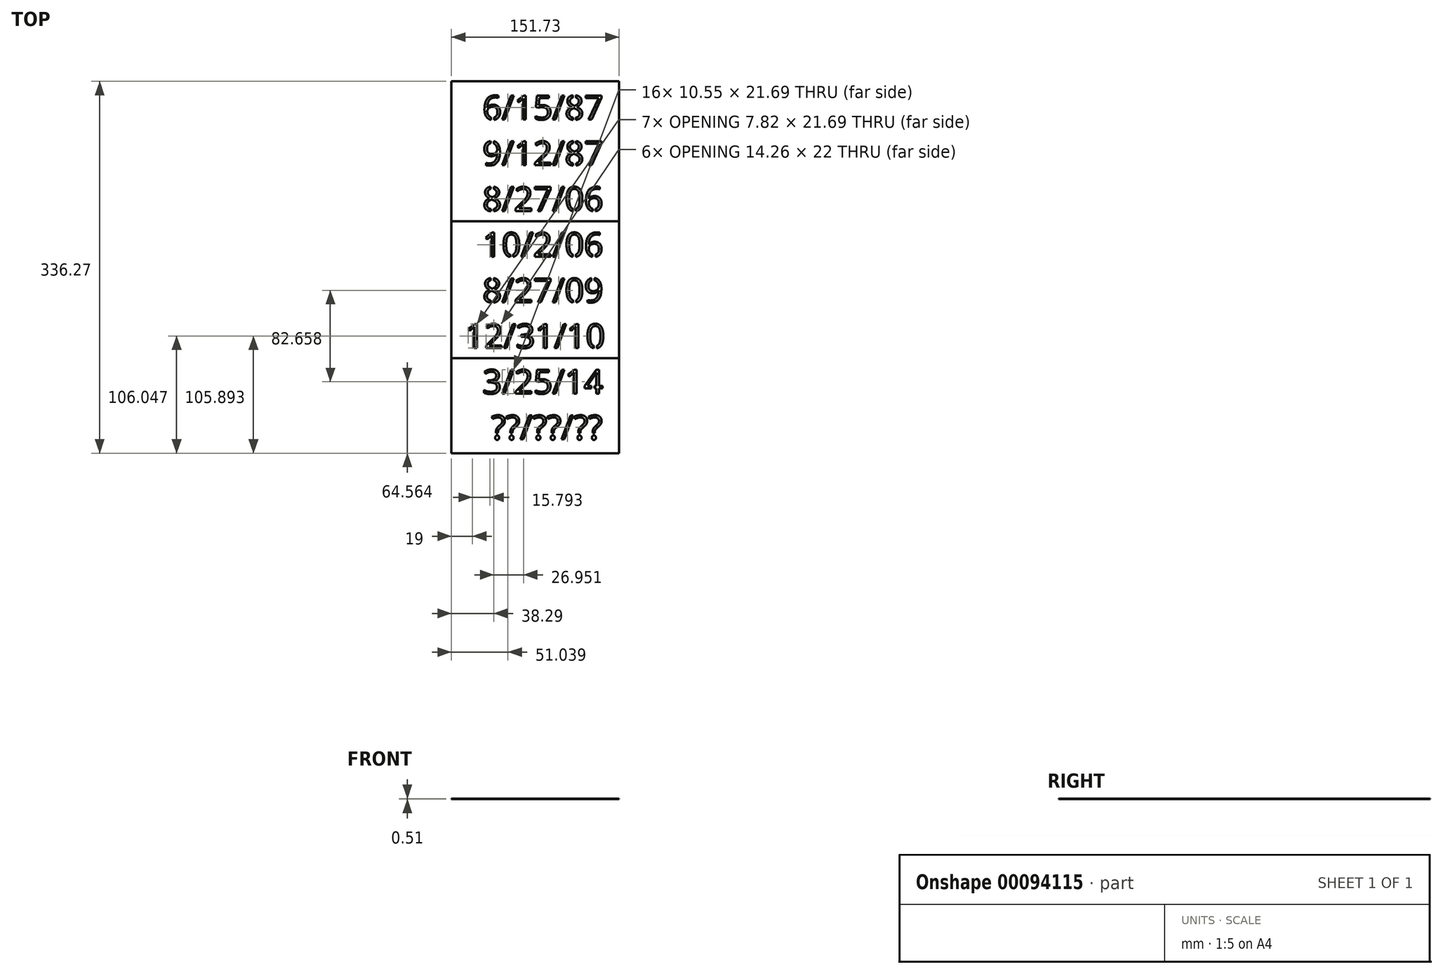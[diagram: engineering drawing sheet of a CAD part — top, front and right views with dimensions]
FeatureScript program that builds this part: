
annotation { "Feature Type Name" : "Feature", "Feature Type Description" : "" }
export const myFeature = defineFeature(function(context is Context, id is Id, definition is map)
    precondition{}
    {
        {
            var Q0;
            Q0=qCreatedBy(makeId("Top.planeOp"),FACE);
            var sketch = newSketch(context, id + "F0", { "sketchPlane" : qUnion([Q0])});
            skText(sketch, "E0", { "text": "  6/15/87\n  9/12/87\n  8/27/06\n  10/2/06\n  8/27/09\n12/31/10\n  3/25/14\n   ??/??/??", "fontName": "OpenSans-Regular.ttf"});
            skLineSegment(sketch, "E1.bottom", {"start": v(-12.3, 34.58) * mm, "end": v(139.43, 34.58) * mm});
            skLineSegment(sketch, "E1.top", {"start": v(-12.3, -301.7) * mm, "end": v(139.43, -301.7) * mm});
            skLineSegment(sketch, "E1.left", {"start": v(-12.3, 34.58) * mm, "end": v(-12.3, -301.7) * mm});
            skLineSegment(sketch, "E1.right", {"start": v(139.43, 34.58) * mm, "end": v(139.43, -301.7) * mm});
            skLineSegment(sketch, "E2", {"start": v(-12.3, -91.86) * mm, "end": v(139.43, -91.86) * mm});
            skLineSegment(sketch, "E3", {"start": v(-12.3, -215.95) * mm, "end": v(139.43, -215.95) * mm});
            skLineSegment(sketch, "E4.left", {"start": v(23.37, 3.55) * mm, "end": v(23.37, -2.65) * mm});
            skLineSegment(sketch, "E4.right", {"start": v(26.12, 3.55) * mm, "end": v(26.12, -2.65) * mm});
            skLineSegment(sketch, "E5.left", {"start": v(97.64, 3.6) * mm, "end": v(97.64, -2.6) * mm});
            skLineSegment(sketch, "E5.right", {"start": v(100.4, 3.6) * mm, "end": v(100.4, -2.6) * mm});
            skLineSegment(sketch, "E6.left", {"start": v(97.5, 23.74) * mm, "end": v(97.5, 17.54) * mm});
            skLineSegment(sketch, "E6.right", {"start": v(100.25, 23.74) * mm, "end": v(100.25, 17.54) * mm});
            skLineSegment(sketch, "E7.left", {"start": v(23.05, -16.8) * mm, "end": v(23.05, -23) * mm});
            skLineSegment(sketch, "E7.right", {"start": v(25.8, -16.8) * mm, "end": v(25.8, -23) * mm});
            skLineSegment(sketch, "E8.left", {"start": v(97.72, -37.6) * mm, "end": v(97.72, -43.8) * mm});
            skLineSegment(sketch, "E8.right", {"start": v(100.47, -37.6) * mm, "end": v(100.47, -43.8) * mm});
            skLineSegment(sketch, "E9.left", {"start": v(97.58, -17.46) * mm, "end": v(97.58, -23.66) * mm});
            skLineSegment(sketch, "E9.right", {"start": v(100.33, -17.46) * mm, "end": v(100.33, -23.66) * mm});
            skLineSegment(sketch, "E10.left", {"start": v(23.27, -79.53) * mm, "end": v(23.27, -85.73) * mm});
            skLineSegment(sketch, "E10.right", {"start": v(26.03, -79.53) * mm, "end": v(26.03, -85.73) * mm});
            skLineSegment(sketch, "E11.left", {"start": v(23.13, -59.4) * mm, "end": v(23.13, -65.6) * mm});
            skLineSegment(sketch, "E11.right", {"start": v(25.89, -59.4) * mm, "end": v(25.89, -65.6) * mm});
            skLineSegment(sketch, "E12.left", {"start": v(115.4, -78.82) * mm, "end": v(115.4, -85.02) * mm});
            skLineSegment(sketch, "E12.right", {"start": v(118.15, -78.82) * mm, "end": v(118.15, -85.02) * mm});
            skLineSegment(sketch, "E13.left", {"start": v(97.58, -78.61) * mm, "end": v(97.58, -84.8) * mm});
            skLineSegment(sketch, "E13.right", {"start": v(100.33, -78.61) * mm, "end": v(100.33, -84.8) * mm});
            skLineSegment(sketch, "E14.left", {"start": v(40.8, -120.16) * mm, "end": v(40.8, -126.36) * mm});
            skLineSegment(sketch, "E14.right", {"start": v(43.56, -120.16) * mm, "end": v(43.56, -126.36) * mm});
            skLineSegment(sketch, "E15.left", {"start": v(97.56, -120.04) * mm, "end": v(97.56, -126.23) * mm});
            skLineSegment(sketch, "E15.right", {"start": v(100.31, -120.04) * mm, "end": v(100.31, -126.23) * mm});
            skLineSegment(sketch, "E16.left", {"start": v(115.23, -119.9) * mm, "end": v(115.23, -126.1) * mm});
            skLineSegment(sketch, "E16.right", {"start": v(117.98, -119.9) * mm, "end": v(117.98, -126.1) * mm});
            skLineSegment(sketch, "E17.left", {"start": v(97.82, -161.57) * mm, "end": v(97.82, -167.76) * mm});
            skLineSegment(sketch, "E17.right", {"start": v(100.57, -161.57) * mm, "end": v(100.57, -167.76) * mm});
            skLineSegment(sketch, "E18.left", {"start": v(114.33, -141.06) * mm, "end": v(114.33, -147.26) * mm});
            skLineSegment(sketch, "E18.right", {"start": v(117.08, -141.06) * mm, "end": v(117.08, -147.26) * mm});
            skLineSegment(sketch, "E19.left", {"start": v(23.14, -141.32) * mm, "end": v(23.14, -147.52) * mm});
            skLineSegment(sketch, "E19.right", {"start": v(25.9, -141.32) * mm, "end": v(25.9, -147.52) * mm});
            skLineSegment(sketch, "E20.left", {"start": v(23.14, -161.7) * mm, "end": v(23.14, -167.9) * mm});
            skLineSegment(sketch, "E20.right", {"start": v(25.9, -161.7) * mm, "end": v(25.9, -167.9) * mm});
            skLineSegment(sketch, "E21.left", {"start": v(114.19, -238.95) * mm, "end": v(114.19, -245.15) * mm});
            skLineSegment(sketch, "E21.right", {"start": v(116.94, -238.95) * mm, "end": v(116.94, -245.15) * mm});
            skLineSegment(sketch, "E22.left", {"start": v(116.57, -202.43) * mm, "end": v(116.57, -208.63) * mm});
            skLineSegment(sketch, "E22.right", {"start": v(119.32, -202.43) * mm, "end": v(119.32, -208.63) * mm});
            const initialGuessF0  = {"E0": [0, 0, 1, 0, 0.02188]};
            skSetInitialGuess(sketch, initialGuessF0);
            skSolve(sketch);
        }
        {
            var Q0;
            Q0=makeQuery(id+"F0.imprint","IMPRINT",FACE,{"disambiguationData":[TD([[makeQuery(id+"F0.imprint","IMPRINT",EDGE,{"derivedFrom":sQuery(id+"F0.wireOp",EDGE,"E0.sketch_text.stroke-0")}),1.0]])]});
            var Q1;
            {var subQ0=sQuery(id+"F0.wireOp",EDGE,"E0.sketch_text.stroke-224");Q1=makeQuery(id+"F0.imprint","IMPRINT",FACE,{"disambiguationData":[TD([[makeQuery(id+"F0.imprint","IMPRINT",EDGE,{"derivedFrom":subQ0}),1.0]])]});}
            var Q2;
            {var subQ5=sQuery(id+"F0.wireOp",EDGE,"E0.sketch_text.stroke-215");Q2=makeQuery(id+"F0.imprint","IMPRINT",FACE,{"disambiguationData":[TD([[makeQuery(id+"F0.imprint","IMPRINT",EDGE,{"derivedFrom":subQ5}),1.0]])]});}
            var Q3;
            {var subQ5=sQuery(id+"F0.wireOp",EDGE,"E0.sketch_text.stroke-274");Q3=makeQuery(id+"F0.imprint","IMPRINT",FACE,{"disambiguationData":[TD([[makeQuery(id+"F0.imprint","IMPRINT",EDGE,{"derivedFrom":subQ5}),1.0]])]});}
            var Q4;
            {var subQ6=sQuery(id+"F0.wireOp",EDGE,"E0.sketch_text.stroke-298");Q4=makeQuery(id+"F0.imprint","IMPRINT",FACE,{"disambiguationData":[TD([[makeQuery(id+"F0.imprint","IMPRINT",EDGE,{"derivedFrom":subQ6}),1.0]])]});}
            var Q5;
            {var subQ5=sQuery(id+"F0.wireOp",EDGE,"E0.sketch_text.stroke-177");Q5=makeQuery(id+"F0.imprint","IMPRINT",FACE,{"disambiguationData":[TD([[makeQuery(id+"F0.imprint","IMPRINT",EDGE,{"derivedFrom":subQ5}),1.0]])]});}
            var Q6;
            {var subQ0=sQuery(id+"F0.wireOp",EDGE,"E0.sketch_text.stroke-186");Q6=makeQuery(id+"F0.imprint","IMPRINT",FACE,{"disambiguationData":[TD([[makeQuery(id+"F0.imprint","IMPRINT",EDGE,{"derivedFrom":subQ0}),1.0]])]});}
            var Q7;
            {var subQ1=sQuery(id+"F0.wireOp",EDGE,"E0.sketch_text.stroke-116");Q7=makeQuery(id+"F0.imprint","IMPRINT",FACE,{"disambiguationData":[TD([[makeQuery(id+"F0.imprint","IMPRINT",EDGE,{"derivedFrom":subQ1}),1.0]])]});}
            var Q8;
            {var subQ5=sQuery(id+"F0.wireOp",EDGE,"E0.sketch_text.stroke-16");Q8=makeQuery(id+"F0.imprint","IMPRINT",FACE,{"disambiguationData":[TD([[makeQuery(id+"F0.imprint","IMPRINT",EDGE,{"derivedFrom":subQ5}),1.0]])]});}
            var Q9;
            {var subQ0=sQuery(id+"F0.wireOp",EDGE,"E0.sketch_text.stroke-85");Q9=makeQuery(id+"F0.imprint","IMPRINT",FACE,{"disambiguationData":[TD([[makeQuery(id+"F0.imprint","IMPRINT",EDGE,{"derivedFrom":subQ0}),1.0]])]});}
            var Q10;
            {var subQ5=sQuery(id+"F0.wireOp",EDGE,"E0.sketch_text.stroke-76");Q10=makeQuery(id+"F0.imprint","IMPRINT",FACE,{"disambiguationData":[TD([[makeQuery(id+"F0.imprint","IMPRINT",EDGE,{"derivedFrom":subQ5}),1.0]])]});}
            var Q11;
            {var subQ5=sQuery(id+"F0.wireOp",EDGE,"E0.sketch_text.stroke-13");var subQ6=sQuery(id+"F0.wireOp",EDGE,"E0.sketch_text.stroke-12");var subQ7=makeQuery(id+"F0.imprint","INTERSECT",VERTEX,{"derivedFrom":[subQ6,subQ5]});Q11=makeQuery(id+"F0.imprint","IMPRINT",FACE,{"disambiguationData":[TD([[makeQuery(id+"F0.imprint","IMPRINT",EDGE,{"disambiguationData":[TD([[subQ7,1.0]])],"derivedFrom":subQ6}),-1.0]])]});}
            var Q12;
            {var subQ5=sQuery(id+"F0.wireOp",EDGE,"E0.sketch_text.stroke-75");var subQ6=sQuery(id+"F0.wireOp",EDGE,"E0.sketch_text.stroke-61");var subQ7=makeQuery(id+"F0.imprint","INTERSECT",VERTEX,{"derivedFrom":[subQ6,subQ5]});Q12=makeQuery(id+"F0.imprint","IMPRINT",FACE,{"disambiguationData":[TD([[makeQuery(id+"F0.imprint","IMPRINT",EDGE,{"disambiguationData":[TD([[subQ7,-1.0]])],"derivedFrom":subQ6}),-1.0]])]});}
            var Q13;
            {var subQ7=sQuery(id+"F0.wireOp",EDGE,"E0.sketch_text.stroke-69");var subQ8=sQuery(id+"F0.wireOp",EDGE,"E0.sketch_text.stroke-68");var subQ9=makeQuery(id+"F0.imprint","INTERSECT",VERTEX,{"derivedFrom":[subQ8,subQ7]});Q13=makeQuery(id+"F0.imprint","IMPRINT",FACE,{"disambiguationData":[TD([[makeQuery(id+"F0.imprint","IMPRINT",EDGE,{"disambiguationData":[TD([[subQ9,1.0]])],"derivedFrom":subQ8}),-1.0]])]});}
            var Q14;
            {var subQ7=sQuery(id+"F0.wireOp",EDGE,"E0.sketch_text.stroke-176");var subQ8=sQuery(id+"F0.wireOp",EDGE,"E0.sketch_text.stroke-162");var subQ9=makeQuery(id+"F0.imprint","INTERSECT",VERTEX,{"derivedFrom":[subQ8,subQ7]});Q14=makeQuery(id+"F0.imprint","IMPRINT",FACE,{"disambiguationData":[TD([[makeQuery(id+"F0.imprint","IMPRINT",EDGE,{"disambiguationData":[TD([[subQ9,-1.0]])],"derivedFrom":subQ8}),-1.0]])]});}
            var Q15;
            {var subQ7=sQuery(id+"F0.wireOp",EDGE,"E0.sketch_text.stroke-112");var subQ8=sQuery(id+"F0.wireOp",EDGE,"E0.sketch_text.stroke-111");var subQ9=makeQuery(id+"F0.imprint","INTERSECT",VERTEX,{"derivedFrom":[subQ8,subQ7]});Q15=makeQuery(id+"F0.imprint","IMPRINT",FACE,{"disambiguationData":[TD([[makeQuery(id+"F0.imprint","IMPRINT",EDGE,{"disambiguationData":[TD([[subQ9,1.0]])],"derivedFrom":subQ8}),-1.0]])]});}
            var Q16;
            {var subQ7=sQuery(id+"F0.wireOp",EDGE,"E0.sketch_text.stroke-170");var subQ8=sQuery(id+"F0.wireOp",EDGE,"E0.sketch_text.stroke-169");var subQ9=makeQuery(id+"F0.imprint","INTERSECT",VERTEX,{"derivedFrom":[subQ8,subQ7]});Q16=makeQuery(id+"F0.imprint","IMPRINT",FACE,{"disambiguationData":[TD([[makeQuery(id+"F0.imprint","IMPRINT",EDGE,{"disambiguationData":[TD([[subQ9,1.0]])],"derivedFrom":subQ8}),-1.0]])]});}
            var Q17;
            {var subQ5=sQuery(id+"F0.wireOp",EDGE,"E0.sketch_text.stroke-295");var subQ6=sQuery(id+"F0.wireOp",EDGE,"E0.sketch_text.stroke-294");var subQ7=makeQuery(id+"F0.imprint","INTERSECT",VERTEX,{"derivedFrom":[subQ6,subQ5]});Q17=makeQuery(id+"F0.imprint","IMPRINT",FACE,{"disambiguationData":[TD([[makeQuery(id+"F0.imprint","IMPRINT",EDGE,{"disambiguationData":[TD([[subQ7,1.0]])],"derivedFrom":subQ6}),-1.0]])]});}
            var Q18;
            {var subQ7=sQuery(id+"F0.wireOp",EDGE,"E0.sketch_text.stroke-268");var subQ8=sQuery(id+"F0.wireOp",EDGE,"E0.sketch_text.stroke-267");var subQ9=makeQuery(id+"F0.imprint","INTERSECT",VERTEX,{"derivedFrom":[subQ8,subQ7]});Q18=makeQuery(id+"F0.imprint","IMPRINT",FACE,{"disambiguationData":[TD([[makeQuery(id+"F0.imprint","IMPRINT",EDGE,{"disambiguationData":[TD([[subQ9,1.0]])],"derivedFrom":subQ8}),-1.0]])]});}
            var Q19;
            {var subQ7=sQuery(id+"F0.wireOp",EDGE,"E0.sketch_text.stroke-208");var subQ8=sQuery(id+"F0.wireOp",EDGE,"E0.sketch_text.stroke-207");var subQ9=makeQuery(id+"F0.imprint","INTERSECT",VERTEX,{"derivedFrom":[subQ8,subQ7]});Q19=makeQuery(id+"F0.imprint","IMPRINT",FACE,{"disambiguationData":[TD([[makeQuery(id+"F0.imprint","IMPRINT",EDGE,{"disambiguationData":[TD([[subQ9,1.0]])],"derivedFrom":subQ8}),-1.0]])]});}
            var Q20;
            {var subQ5=sQuery(id+"F0.wireOp",EDGE,"E0.sketch_text.stroke-214");var subQ6=sQuery(id+"F0.wireOp",EDGE,"E0.sketch_text.stroke-200");var subQ7=makeQuery(id+"F0.imprint","INTERSECT",VERTEX,{"derivedFrom":[subQ6,subQ5]});Q20=makeQuery(id+"F0.imprint","IMPRINT",FACE,{"disambiguationData":[TD([[makeQuery(id+"F0.imprint","IMPRINT",EDGE,{"disambiguationData":[TD([[subQ7,-1.0]])],"derivedFrom":subQ6}),-1.0]])]});}
            extrude(context, id + "F1", {"entities" : qUnion([Q0, Q1, Q2, Q3, Q4, Q5, Q6, Q7, Q8, Q9, Q10, Q11, Q12, Q13, Q14, Q15, Q16, Q17, Q18, Q19, Q20]), "depth" : 0.5 * mm});
        }
        {
            var Q0;
            Q0=makeQuery(id+"F0.imprint","IMPRINT",FACE,{"disambiguationData":[TD([[makeQuery(id+"F0.imprint","IMPRINT",EDGE,{"derivedFrom":sQuery(id+"F0.wireOp",EDGE,"E0.sketch_text.stroke-307")}),1.0]])]});
            var Q1;
            {var subQ5=sQuery(id+"F0.wireOp",EDGE,"E0.sketch_text.stroke-324");Q1=makeQuery(id+"F0.imprint","IMPRINT",FACE,{"disambiguationData":[TD([[makeQuery(id+"F0.imprint","IMPRINT",EDGE,{"derivedFrom":subQ5}),1.0]])]});}
            var Q2;
            {var subQ5=sQuery(id+"F0.wireOp",EDGE,"E0.sketch_text.stroke-368");Q2=makeQuery(id+"F0.imprint","IMPRINT",FACE,{"disambiguationData":[TD([[makeQuery(id+"F0.imprint","IMPRINT",EDGE,{"derivedFrom":subQ5}),1.0]])]});}
            var Q3;
            {var subQ4=sQuery(id+"F0.wireOp",EDGE,"E0.sketch_text.stroke-392");Q3=makeQuery(id+"F0.imprint","IMPRINT",FACE,{"disambiguationData":[TD([[makeQuery(id+"F0.imprint","IMPRINT",EDGE,{"derivedFrom":subQ4}),1.0]])]});}
            var Q4;
            {var subQ1=sQuery(id+"F0.wireOp",EDGE,"E0.sketch_text.stroke-500");Q4=makeQuery(id+"F0.imprint","IMPRINT",FACE,{"disambiguationData":[TD([[makeQuery(id+"F0.imprint","IMPRINT",EDGE,{"derivedFrom":subQ1}),1.0]])]});}
            var Q5;
            {var subQ5=sQuery(id+"F0.wireOp",EDGE,"E0.sketch_text.stroke-475");Q5=makeQuery(id+"F0.imprint","IMPRINT",FACE,{"disambiguationData":[TD([[makeQuery(id+"F0.imprint","IMPRINT",EDGE,{"derivedFrom":subQ5}),1.0]])]});}
            var Q6;
            {var subQ0=sQuery(id+"F0.wireOp",EDGE,"E0.sketch_text.stroke-425");Q6=makeQuery(id+"F0.imprint","IMPRINT",FACE,{"disambiguationData":[TD([[makeQuery(id+"F0.imprint","IMPRINT",EDGE,{"derivedFrom":subQ0}),1.0]])]});}
            var Q7;
            {var subQ5=sQuery(id+"F0.wireOp",EDGE,"E0.sketch_text.stroke-416");Q7=makeQuery(id+"F0.imprint","IMPRINT",FACE,{"disambiguationData":[TD([[makeQuery(id+"F0.imprint","IMPRINT",EDGE,{"derivedFrom":subQ5}),1.0]])]});}
            var Q8;
            {var subQ5=sQuery(id+"F0.wireOp",EDGE,"E0.sketch_text.stroke-600");Q8=makeQuery(id+"F0.imprint","IMPRINT",FACE,{"disambiguationData":[TD([[makeQuery(id+"F0.imprint","IMPRINT",EDGE,{"derivedFrom":subQ5}),1.0]])]});}
            var Q9;
            {var subQ7=sQuery(id+"F0.wireOp",EDGE,"E0.sketch_text.stroke-318");var subQ8=sQuery(id+"F0.wireOp",EDGE,"E0.sketch_text.stroke-317");var subQ9=makeQuery(id+"F0.imprint","INTERSECT",VERTEX,{"derivedFrom":[subQ8,subQ7]});Q9=makeQuery(id+"F0.imprint","IMPRINT",FACE,{"disambiguationData":[TD([[makeQuery(id+"F0.imprint","IMPRINT",EDGE,{"disambiguationData":[TD([[subQ9,1.0]])],"derivedFrom":subQ8}),-1.0]])]});}
            var Q10;
            {var subQ5=sQuery(id+"F0.wireOp",EDGE,"E0.sketch_text.stroke-415");var subQ6=sQuery(id+"F0.wireOp",EDGE,"E0.sketch_text.stroke-401");var subQ7=makeQuery(id+"F0.imprint","INTERSECT",VERTEX,{"derivedFrom":[subQ6,subQ5]});Q10=makeQuery(id+"F0.imprint","IMPRINT",FACE,{"disambiguationData":[TD([[makeQuery(id+"F0.imprint","IMPRINT",EDGE,{"disambiguationData":[TD([[subQ7,-1.0]])],"derivedFrom":subQ6}),-1.0]])]});}
            var Q11;
            {var subQ7=sQuery(id+"F0.wireOp",EDGE,"E0.sketch_text.stroke-408");var subQ9=sQuery(id+"F0.wireOp",EDGE,"E0.sketch_text.stroke-409");var subQ10=makeQuery(id+"F0.imprint","INTERSECT",VERTEX,{"derivedFrom":[subQ7,subQ9]});Q11=makeQuery(id+"F0.imprint","IMPRINT",FACE,{"disambiguationData":[TD([[makeQuery(id+"F0.imprint","IMPRINT",EDGE,{"disambiguationData":[TD([[subQ10,1.0]])],"derivedFrom":subQ7}),-1.0]])]});}
            var Q12;
            {var subQ7=sQuery(id+"F0.wireOp",EDGE,"E0.sketch_text.stroke-469");var subQ8=sQuery(id+"F0.wireOp",EDGE,"E0.sketch_text.stroke-468");var subQ9=makeQuery(id+"F0.imprint","INTERSECT",VERTEX,{"derivedFrom":[subQ8,subQ7]});Q12=makeQuery(id+"F0.imprint","IMPRINT",FACE,{"disambiguationData":[TD([[makeQuery(id+"F0.imprint","IMPRINT",EDGE,{"disambiguationData":[TD([[subQ9,1.0]])],"derivedFrom":subQ8}),-1.0]])]});}
            var Q13;
            {var subQ5=sQuery(id+"F0.wireOp",EDGE,"E0.sketch_text.stroke-496");var subQ7=sQuery(id+"F0.wireOp",EDGE,"E0.sketch_text.stroke-495");var subQ8=makeQuery(id+"F0.imprint","INTERSECT",VERTEX,{"derivedFrom":[subQ7,subQ5]});Q13=makeQuery(id+"F0.imprint","IMPRINT",FACE,{"disambiguationData":[TD([[makeQuery(id+"F0.imprint","IMPRINT",EDGE,{"disambiguationData":[TD([[subQ8,1.0]])],"derivedFrom":subQ7}),-1.0]])]});}
            var Q14;
            {var subQ7=sQuery(id+"F0.wireOp",EDGE,"E0.sketch_text.stroke-388");var subQ9=sQuery(id+"F0.wireOp",EDGE,"E0.sketch_text.stroke-389");var subQ10=makeQuery(id+"F0.imprint","INTERSECT",VERTEX,{"derivedFrom":[subQ7,subQ9]});Q14=makeQuery(id+"F0.imprint","IMPRINT",FACE,{"disambiguationData":[TD([[makeQuery(id+"F0.imprint","IMPRINT",EDGE,{"disambiguationData":[TD([[subQ10,1.0]])],"derivedFrom":subQ7}),-1.0]])]});}
            var Q15;
            {var subQ5=sQuery(id+"F0.wireOp",EDGE,"E0.sketch_text.stroke-362");var subQ6=sQuery(id+"F0.wireOp",EDGE,"E0.sketch_text.stroke-361");var subQ7=makeQuery(id+"F0.imprint","INTERSECT",VERTEX,{"derivedFrom":[subQ6,subQ5]});Q15=makeQuery(id+"F0.imprint","IMPRINT",FACE,{"disambiguationData":[TD([[makeQuery(id+"F0.imprint","IMPRINT",EDGE,{"disambiguationData":[TD([[subQ7,1.0]])],"derivedFrom":subQ6}),-1.0]])]});}
            var Q16;
            {var subQ5=sQuery(id+"F0.wireOp",EDGE,"E0.sketch_text.stroke-594");var subQ6=sQuery(id+"F0.wireOp",EDGE,"E0.sketch_text.stroke-593");var subQ7=makeQuery(id+"F0.imprint","INTERSECT",VERTEX,{"derivedFrom":[subQ6,subQ5]});Q16=makeQuery(id+"F0.imprint","IMPRINT",FACE,{"disambiguationData":[TD([[makeQuery(id+"F0.imprint","IMPRINT",EDGE,{"disambiguationData":[TD([[subQ7,1.0]])],"derivedFrom":subQ6}),-1.0]])]});}
            extrude(context, id + "F2", {"entities" : qUnion([Q0, Q1, Q2, Q3, Q4, Q5, Q6, Q7, Q8, Q9, Q10, Q11, Q12, Q13, Q14, Q15, Q16]), "depth" : 0.5 * mm});
        }
        {
            var Q0;
            Q0=makeQuery(id+"F0.imprint","IMPRINT",FACE,{"disambiguationData":[TD([[makeQuery(id+"F0.imprint","IMPRINT",EDGE,{"derivedFrom":sQuery(id+"F0.wireOp",EDGE,"E0.sketch_text.stroke-608")}),1.0]])]});
            var Q1;
            {var subQ1=sQuery(id+"F0.wireOp",EDGE,"E0.sketch_text.stroke-703");Q1=makeQuery(id+"F0.imprint","IMPRINT",FACE,{"disambiguationData":[TD([[makeQuery(id+"F0.imprint","IMPRINT",EDGE,{"derivedFrom":subQ1}),1.0]])]});}
            var Q2;
            {var subQ0=sQuery(id+"F0.wireOp",EDGE,"E21.right");var subQ1=sQuery(id+"F0.wireOp",EDGE,"E0.sketch_text.stroke-696");var subQ2=makeQuery(id+"F0.imprint","INTERSECT",VERTEX,{"derivedFrom":[subQ1,subQ0]});Q2=makeQuery(id+"F0.imprint","IMPRINT",FACE,{"disambiguationData":[TD([[makeQuery(id+"F0.imprint","IMPRINT",EDGE,{"disambiguationData":[TD([[subQ2,-1.0]])],"derivedFrom":subQ1}),-1.0]])]});}
            extrude(context, id + "F3", {"entities" : qUnion([Q0, Q1, Q2]), "depth" : 0.5 * mm});
        }
    });
